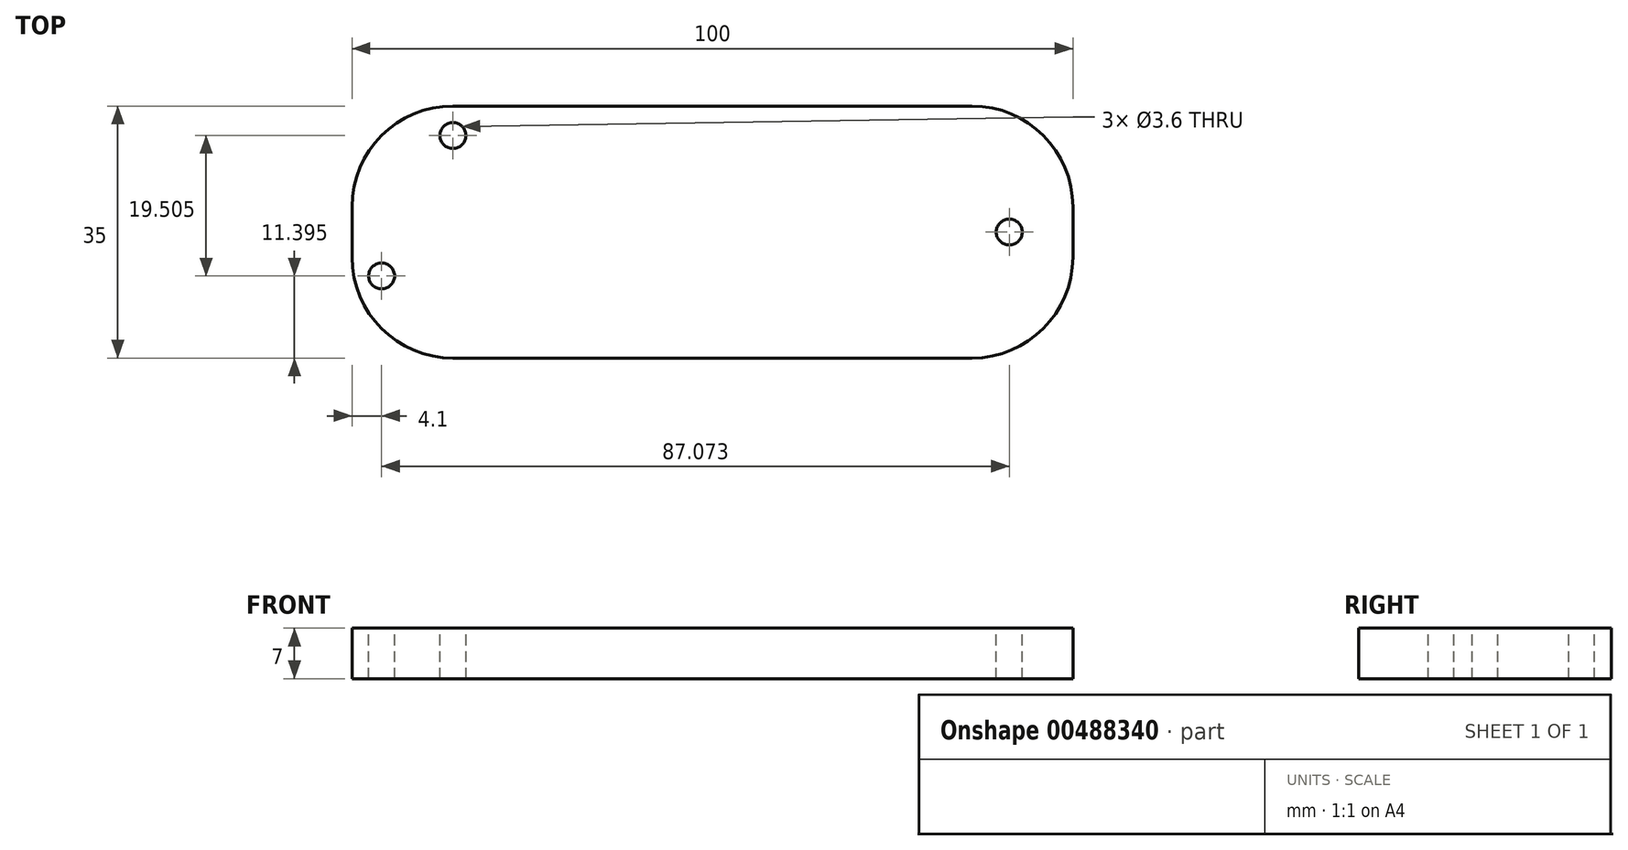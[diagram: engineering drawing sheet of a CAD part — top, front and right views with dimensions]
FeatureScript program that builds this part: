
annotation { "Feature Type Name" : "Feature", "Feature Type Description" : "" }
export const myFeature = defineFeature(function(context is Context, id is Id, definition is map)
    precondition{}
    {
        {
            var Q0;
            Q0=qCreatedBy(makeId("Top.planeOp"),FACE);
            var sketch = newSketch(context, id + "F0", { "sketchPlane" : qUnion([Q0])});
            skLineSegment(sketch, "E0.bottom", {"start": v(36, 17.5) * mm, "end": v(-36, 17.5) * mm});
            skLineSegment(sketch, "E0.top", {"start": v(36, -17.5) * mm, "end": v(-36, -17.5) * mm});
            skLineSegment(sketch, "E0.left", {"start": v(50, 3.5) * mm, "end": v(50, -3.5) * mm});
            skLineSegment(sketch, "E0.right", {"start": v(-50, 3.5) * mm, "end": v(-50, -3.5) * mm});
            skPoint(sketch, "E0.middle", {"position": v(0, 0) * mm});
            skPoint(sketch, "E1.visualSharp", {"position": v(-50, -17.5) * mm});
            skArc(sketch, "E1.filletArc", {"start": v(-50, -3.5) * mm, "mid": v(-45.9, -13.4) * mm, "end": v(-36, -17.5) * mm});
            skPoint(sketch, "E2.visualSharp", {"position": v(-50, 17.5) * mm});
            skArc(sketch, "E2.filletArc", {"start": v(-36, 17.5) * mm, "mid": v(-45.9, 13.4) * mm, "end": v(-50, 3.5) * mm});
            skPoint(sketch, "E3.visualSharp", {"position": v(50, -17.5) * mm});
            skArc(sketch, "E3.filletArc", {"start": v(36, -17.5) * mm, "mid": v(45.9, -13.4) * mm, "end": v(50, -3.5) * mm});
            skPoint(sketch, "E4.visualSharp", {"position": v(50, 17.5) * mm});
            skArc(sketch, "E4.filletArc", {"start": v(50, 3.5) * mm, "mid": v(45.9, 13.4) * mm, "end": v(36, 17.5) * mm});
            skSolve(sketch);
        }
        {
            var Q0;
            Q0 = qSketchRegion(id + "F0", true);
            extrude(context, id + "F1", {"entities" : qUnion([Q0]), "endBound" : BoundingType.SYMMETRIC, "depth" : 7 * mm});
        }
        {
            var Q0;
            Q0=makeQuery(id+"F1.opExtrude","CAP_FACE",FACE,{"disambiguationData":[OSD([sQuery(id+"F0.wireOp",EDGE,"E0.bottom"),sQuery(id+"F0.wireOp",EDGE,"E0.top"),sQuery(id+"F0.wireOp",EDGE,"E0.left"),sQuery(id+"F0.wireOp",EDGE,"E0.right"),sQuery(id+"F0.wireOp",EDGE,"E1.filletArc"),sQuery(id+"F0.wireOp",EDGE,"E2.filletArc"),sQuery(id+"F0.wireOp",EDGE,"E3.filletArc"),sQuery(id+"F0.wireOp",EDGE,"E4.filletArc")])],"isStart":false});
            var sketch = newSketch(context, id + "F2", { "sketchPlane" : qUnion([Q0])});
            skCircle(sketch, "E5", {"center": v(41.17, 0) * mm, "radius": 1.8 * mm});
            skPoint(sketch, "E5.centerSnap0", {"position": v(50, 0) * mm});
            skSolve(sketch);
        }
        {
            var Q0;
            Q0 = qSketchRegion(id + "F2", true);
            extrude(context, id + "F3", {"entities" : qUnion([Q0]), "operationType" : NewBodyOperationType.REMOVE, "oppositeDirection" : true, "depth" : 8 * mm});
        }
        {
            var Q0;
            Q0=makeQuery(id+"F1.opExtrude","CAP_FACE",FACE,{"disambiguationData":[OSD([sQuery(id+"F0.wireOp",EDGE,"E0.bottom"),sQuery(id+"F0.wireOp",EDGE,"E0.top"),sQuery(id+"F0.wireOp",EDGE,"E0.left"),sQuery(id+"F0.wireOp",EDGE,"E0.right"),sQuery(id+"F0.wireOp",EDGE,"E1.filletArc"),sQuery(id+"F0.wireOp",EDGE,"E2.filletArc"),sQuery(id+"F0.wireOp",EDGE,"E3.filletArc"),sQuery(id+"F0.wireOp",EDGE,"E4.filletArc")])],"isStart":false});
            var sketch = newSketch(context, id + "F4", { "sketchPlane" : qUnion([Q0])});
            skPoint(sketch, "E6.centerSnap0", {"position": v(-45.9, 13.4) * mm});
            skCircle(sketch, "E7", {"center": v(-45.9, -6.1) * mm, "radius": 1.8 * mm});
            skPoint(sketch, "E7.centerSnap0", {"position": v(-45.9, -13.4) * mm});
            skSolve(sketch);
        }
        {
            var Q0;
            Q0 = qSketchRegion(id + "F4", true);
            extrude(context, id + "F5", {"entities" : qUnion([Q0]), "operationType" : NewBodyOperationType.REMOVE, "oppositeDirection" : true, "depth" : 7 * mm});
        }
        {
            var Q0;
            Q0=makeQuery(id+"F1.opExtrude","CAP_FACE",FACE,{"disambiguationData":[OSD([sQuery(id+"F0.wireOp",EDGE,"E0.bottom"),sQuery(id+"F0.wireOp",EDGE,"E0.top"),sQuery(id+"F0.wireOp",EDGE,"E0.left"),sQuery(id+"F0.wireOp",EDGE,"E0.right"),sQuery(id+"F0.wireOp",EDGE,"E1.filletArc"),sQuery(id+"F0.wireOp",EDGE,"E2.filletArc"),sQuery(id+"F0.wireOp",EDGE,"E3.filletArc"),sQuery(id+"F0.wireOp",EDGE,"E4.filletArc")])],"isStart":false});
            var sketch = newSketch(context, id + "F6", { "sketchPlane" : qUnion([Q0])});
            skCircle(sketch, "E8", {"center": v(-36, 13.4) * mm, "radius": 1.8 * mm});
            skPoint(sketch, "E8.centerSnap0", {"position": v(-45.9, 13.4) * mm});
            skSolve(sketch);
        }
        {
            var Q0;
            Q0 = qSketchRegion(id + "F6", true);
            extrude(context, id + "F7", {"entities" : qUnion([Q0]), "operationType" : NewBodyOperationType.REMOVE, "oppositeDirection" : true, "depth" : 7 * mm});
        }
    });
